# Revit family: Door-Access-Best Access Doors-Fire_Rated_Insulated_Upward_Opening-BA-FRU
name_source: partatom
category: Specialty Equipment
revit_build: Autodesk Revit 2017 (Build: 20160225_1515(x64)
units: mm (PartAtom-declared; Revit-internal decimal feet)

## family parameters
Cut with Voids When Loaded = No
Host = Face
OmniClass Number = 23.30.10.27.17
Part Type = Normal
Room Calculation Point = No
Round Connector Dimension = Use Diameter
Shared = No

## types (4) — shared parameters
Assembly Code = C1020700
Construction Material = Metal - Best Access Doors - Aluminum
Default Elevation = 0"
Description = Fire Rated Insulated Upward Opening Access Door for Ceiling
Finish = Metal - Best Access Doors - Powder Coated White
Frame Depth = 2 7/8"
Manufacturer = Best Access Doors
Model = BA-FRU
Product data url = https://bimobject.com

## per-type parameters (varying)
| type | Door Height | Door Width | Frame Height | Frame Width | Height Calc | URL | Width Calc |
| Custom | 12" | 12" | 14 1/4" | 14 1/4" | 12" | http://www.bestaccessdoors.com | 12" |
| 22x30 | 30" | 22" | 32 1/4" | 24 1/4" | 30" | https://www.bestaccessdoors.com | 22" |
| 22x36 | 36" | 22" | 38 1/4" | 24 1/4" | 36" | https://www.bestaccessdoors.com | 22" |
| 24x24 | 24" | 24" | 26 1/4" | 26 1/4" | 24" | https://www.bestaccessdoors.com | 24" |

## geometry (parser evidence)
native form markers: Blend x4, Sweep x22
no freeform markers — native parametric forms only
